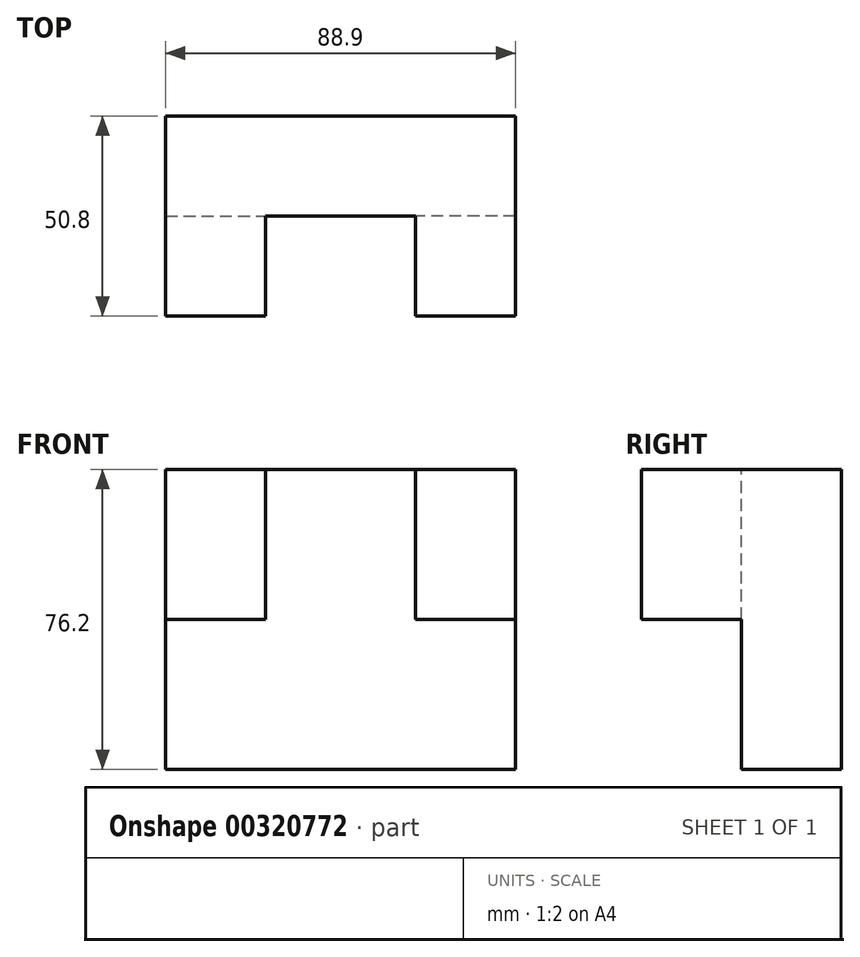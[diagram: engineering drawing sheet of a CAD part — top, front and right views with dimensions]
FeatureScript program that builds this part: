
annotation { "Feature Type Name" : "Feature", "Feature Type Description" : "" }
export const myFeature = defineFeature(function(context is Context, id is Id, definition is map)
    precondition{}
    {
        {
            var Q0;
            Q0=qCreatedBy(makeId("Front.planeOp"),FACE);
            var sketch = newSketch(context, id + "F0", { "sketchPlane" : qUnion([Q0])});
            skLineSegment(sketch, "E0", {"start": v(-46.2, -40.33) * mm, "end": v(42.7, -40.33) * mm});
            skLineSegment(sketch, "E1", {"start": v(42.7, -40.33) * mm, "end": v(42.7, 35.87) * mm});
            skLineSegment(sketch, "E2", {"start": v(42.7, 35.87) * mm, "end": v(-46.2, 35.87) * mm});
            skLineSegment(sketch, "E3", {"start": v(-46.2, 35.87) * mm, "end": v(-46.2, -40.33) * mm});
            skSolve(sketch);
        }
        {
            var Q0;
            Q0=makeQuery(id+"F0.imprint","IMPRINT",FACE,{"disambiguationData":[TD([[makeQuery(id+"F0.imprint","IMPRINT",EDGE,{"derivedFrom":sQuery(id+"F0.wireOp",EDGE,"E0")}),1.0]])]});
            extrude(context, id + "F1", {"entities" : qUnion([Q0]), "depth" : 25.4 * mm});
        }
        {
            var Q0;
            Q0=makeQuery(id+"F1.opExtrude","CAP_FACE",FACE,{"disambiguationData":[OSD([sQuery(id+"F0.wireOp",EDGE,"E0"),sQuery(id+"F0.wireOp",EDGE,"E1"),sQuery(id+"F0.wireOp",EDGE,"E2"),sQuery(id+"F0.wireOp",EDGE,"E3")])],"isStart":false});
            var sketch = newSketch(context, id + "F2", { "sketchPlane" : qUnion([Q0])});
            skLineSegment(sketch, "E4", {"start": v(-46.2, -2.23) * mm, "end": v(-20.8, -2.23) * mm});
            skLineSegment(sketch, "E5", {"start": v(-20.8, -2.23) * mm, "end": v(-20.8, 35.87) * mm});
            skSolve(sketch);
        }
        {
            var Q0;
            {var subQ0=sQuery(id+"F2.wireOp",EDGE,"E4");Q0=makeQuery(id+"F2.imprint","IMPRINT",FACE,{"disambiguationData":[TD([[makeQuery(id+"F2.imprint","IMPRINT",EDGE,{"derivedFrom":subQ0}),1.0]])]});}
            extrude(context, id + "F3", {"entities" : qUnion([Q0]), "operationType" : NewBodyOperationType.ADD, "depth" : 25.4 * mm});
        }
        {
            var Q0;
            Q0=makeQuery(id+"F1.opExtrude","CAP_FACE",FACE,{"disambiguationData":[OSD([sQuery(id+"F0.wireOp",EDGE,"E0"),sQuery(id+"F0.wireOp",EDGE,"E1"),sQuery(id+"F0.wireOp",EDGE,"E2"),sQuery(id+"F0.wireOp",EDGE,"E3")])],"isStart":false});
            var sketch = newSketch(context, id + "F4", { "sketchPlane" : qUnion([Q0])});
            skLineSegment(sketch, "E6", {"start": v(42.7, -2.23) * mm, "end": v(17.3, -2.23) * mm});
            skLineSegment(sketch, "E7", {"start": v(17.3, -2.23) * mm, "end": v(17.3, 35.87) * mm});
            skSolve(sketch);
        }
        {
            var Q0;
            {var subQ0=sQuery(id+"F4.wireOp",EDGE,"E6");Q0=makeQuery(id+"F4.imprint","IMPRINT",FACE,{"disambiguationData":[TD([[makeQuery(id+"F4.imprint","IMPRINT",EDGE,{"derivedFrom":subQ0}),-1.0]])]});}
            extrude(context, id + "F5", {"entities" : qUnion([Q0]), "operationType" : NewBodyOperationType.ADD, "depth" : 25.4 * mm});
        }
    });
